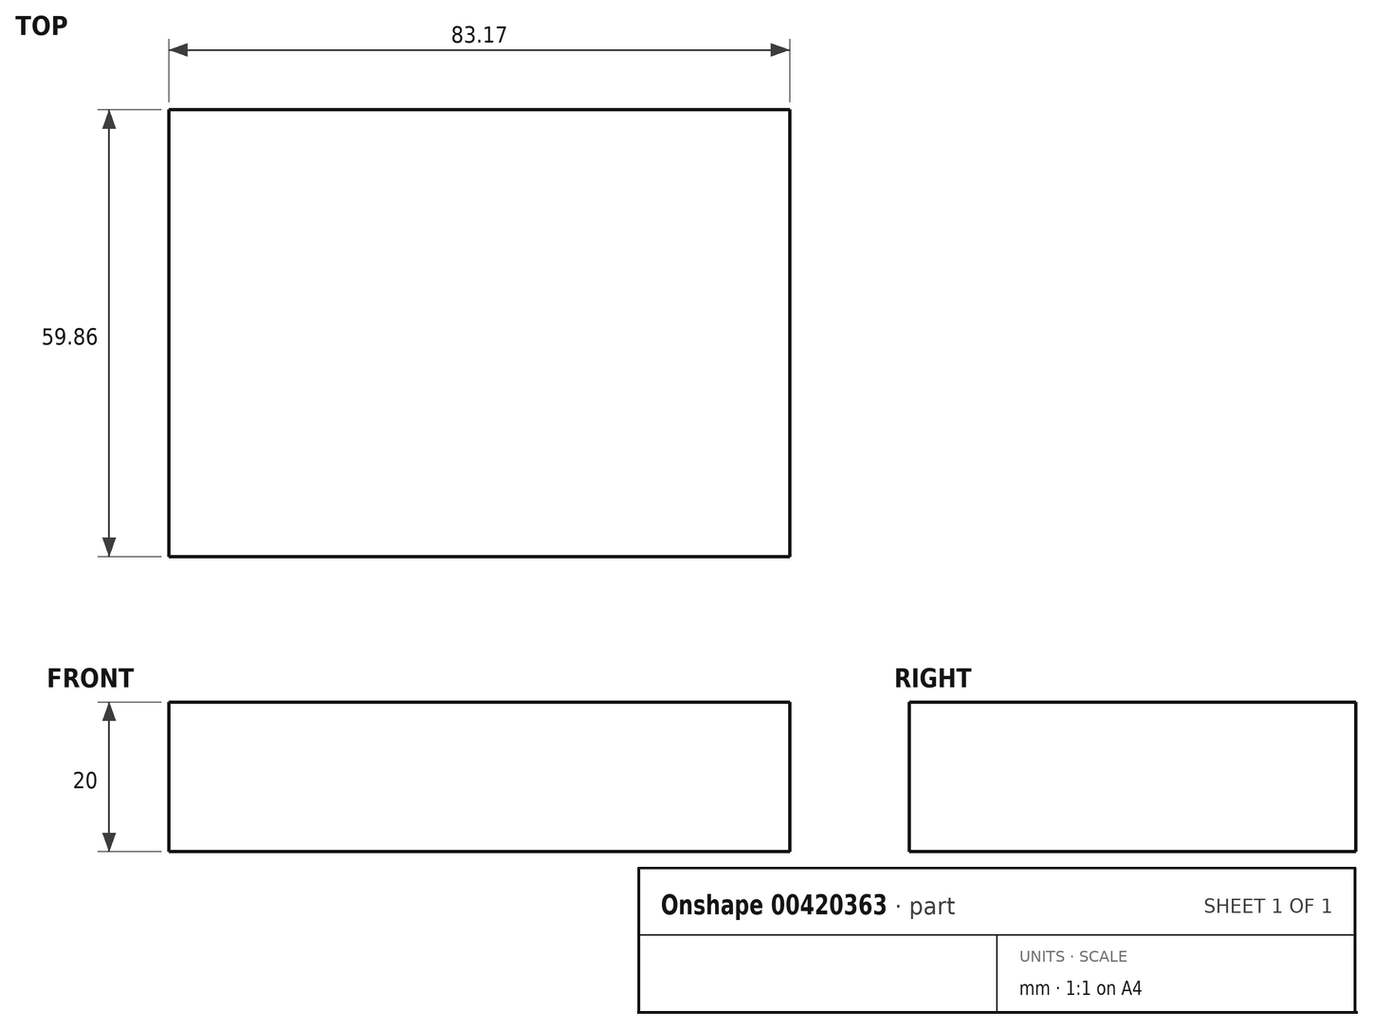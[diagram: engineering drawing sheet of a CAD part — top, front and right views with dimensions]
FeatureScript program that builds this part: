
annotation { "Feature Type Name" : "Feature", "Feature Type Description" : "" }
export const myFeature = defineFeature(function(context is Context, id is Id, definition is map)
    precondition{}
    {
        {
            var Q0;
            Q0=qCreatedBy(makeId("Top.planeOp"),FACE);
            var sketch = newSketch(context, id + "F0", { "sketchPlane" : qUnion([Q0])});
            skLineSegment(sketch, "E0.bottom", {"start": v(-37.41, 24.75) * mm, "end": v(45.76, 24.75) * mm});
            skLineSegment(sketch, "E0.top", {"start": v(-37.41, -35.11) * mm, "end": v(45.76, -35.11) * mm});
            skLineSegment(sketch, "E0.left", {"start": v(-37.41, 24.75) * mm, "end": v(-37.41, -35.11) * mm});
            skLineSegment(sketch, "E0.right", {"start": v(45.76, 24.75) * mm, "end": v(45.76, -35.11) * mm});
            skSolve(sketch);
        }
        {
            var Q0;
            Q0=makeQuery(id+"F0.imprint","IMPRINT",FACE,{"disambiguationData":[TD([[makeQuery(id+"F0.imprint","IMPRINT",EDGE,{"derivedFrom":sQuery(id+"F0.wireOp",EDGE,"E0.bottom")}),-1.0]])]});
            extrude(context, id + "F1", {"entities" : qUnion([Q0]), "depth" : 20 * mm});
        }
    });
